# Revit family: All-Lite ECD-245
name_source: partatom
category: Mechanical Equipment
revit_build: Autodesk Revit 2013 (Build: 20120221_2030(x64)
units: mm (PartAtom-declared; Revit-internal decimal feet)

## types (1)
- All-Lite ECD-245
    Air Volume Delivered @ Beginning Point of Water Penetration = 7744 fpm
    Array = 49
    Assembly Code = B2010300
    Blade Material = <By Category>
    Blade Width = 2' - 10"
    Blades = 0.060'' thick horizontal chevron style
    Center Damper Control = 0' - 0 1/2"
    Cut Sheet = http://alllite.com
    Default Height = 4' - 0"
    Description = The ECD-245 offers exceptional protection against winddriven
rain under the most severe conditions. The ECD-245
incorporates horizontal blades and is available in a wide
array of anodized and painted finishes including custom
color matching.
    Design Load = 20 psf
    Face of Frame From Face of Wall = 0' - 0 1/2"
    Frame = 2'' deep × 0.060'' thick channel
    Frame Material = <By Category>
    Free Area = 48'' × 48'' unit: 6.6 ft2 41.3%
    Free Area Velocity @ Beginning Point of Water Penetration = 1172 fpm
    Height = 5' - 0"
    Height Control = 5' - 0"
    Jamb Height = 4' - 11 1/4"
    Manufacturer = Pottorff
    Max Height = 10' - 0"
    Max Width = 10' - 0"
    Max Width to Center of Damper = 0' - 2 1/2"
    Maximum Size (Multiple Section) = Unlimited
    Maximum Size (Single Section) = 60'' x 120'', 120'' x 60''
    Min Height = 0' - 4"
    Min Width = 0' - 5"
    Minimum Size = 4'' x 5''
    Model = ECD-245
    Mullion = Visible
    Omni Class Code = 22-23 09 13 43
    Omni Class Title = Louver
    Pressure Loss @ Beginning Point of Water Penetration = .37 in.wg.
    Product URL = http://www.alllite.com
    Screen = 1/2'' × 0.063'' expanded and flattened aluminum
    Specifications = http://www.alllite.com
    URL = http://alllite.com
    Velocity @ 0.15 in.wg. Pressure Loss = 760 fpm
    Warranty = http://alllite.com
    Width = 3' - 0"
    Width Control = 3' - 0"

## geometry (parser evidence)
native form markers: Blend x17, Sweep x9
no freeform markers — native parametric forms only
